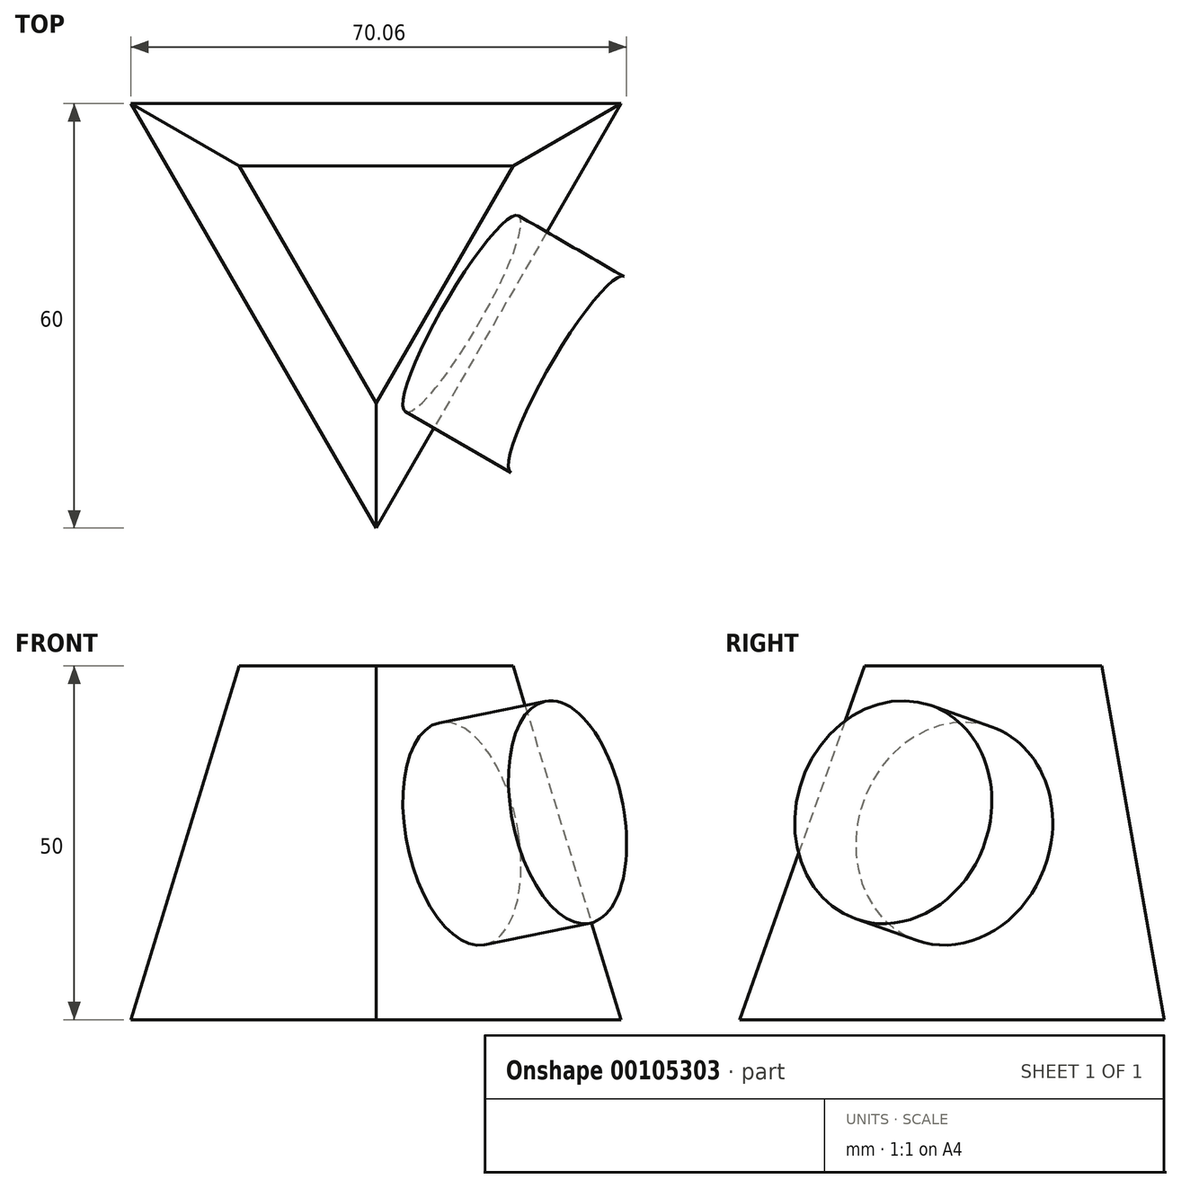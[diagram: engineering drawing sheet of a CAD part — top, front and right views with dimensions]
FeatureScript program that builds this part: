
annotation { "Feature Type Name" : "Feature", "Feature Type Description" : "" }
export const myFeature = defineFeature(function(context is Context, id is Id, definition is map)
    precondition{}
    {
        {
            var Q0;
            Q0=qCreatedBy(makeId("Top.planeOp"),FACE);
            var sketch = newSketch(context, id + "F0", { "sketchPlane" : qUnion([Q0])});
            skLineSegment(sketch, "E0", {"start": v(-34.64, 20) * mm, "end": v(34.64, 20) * mm});
            skLineSegment(sketch, "E1", {"start": v(34.64, 20) * mm, "end": v(0, -40) * mm});
            skLineSegment(sketch, "E2", {"start": v(0, -40) * mm, "end": v(-34.64, 20) * mm});
            skLineSegment(sketch, "E3", {"start": v(-34.64, 20) * mm, "end": v(-34.64, 24.92) * mm});
            skSolve(sketch);
        }
        {
            var Q0;
            Q0 = qSketchRegion(id + "F0", true);
            extrude(context, id + "F1", {"entities" : qUnion([Q0]), "depth" : 50 * mm, "hasDraft" : true, "draftAngle" : 10 * degree, "draftPullDirection" : true});
        }
        {
            var Q0;
            Q0=makeQuery(id+"F1.opExtrude","CAP_FACE",FACE,{"disambiguationData":[OSD([sQuery(id+"F0.wireOp",EDGE,"E0"),sQuery(id+"F0.wireOp",EDGE,"E1"),sQuery(id+"F0.wireOp",EDGE,"E2")])],"isStart":false});
            var sketch = newSketch(context, id + "F2", { "sketchPlane" : qUnion([Q0])});
            skSolve(sketch);
        }
        {
            var Q0;
            Q0=makeQuery(id+"F1.opExtrude","SWEPT_FACE",FACE,{"disambiguationData":[OSD([sQuery(id+"F0.wireOp",EDGE,"E1")])]});
            var sketch = newSketch(context, id + "F3", { "sketchPlane" : qUnion([Q0])});
            skCircle(sketch, "E4", {"center": v(0, 23.34) * mm, "radius": 16 * mm});
            skSolve(sketch);
        }
        {
            var Q0;
            Q0 = qSketchRegion(id + "F3", true);
            extrude(context, id + "F4", {"entities" : qUnion([Q0]), "operationType" : NewBodyOperationType.ADD, "depth" : 17.5 * mm});
        }
    });
